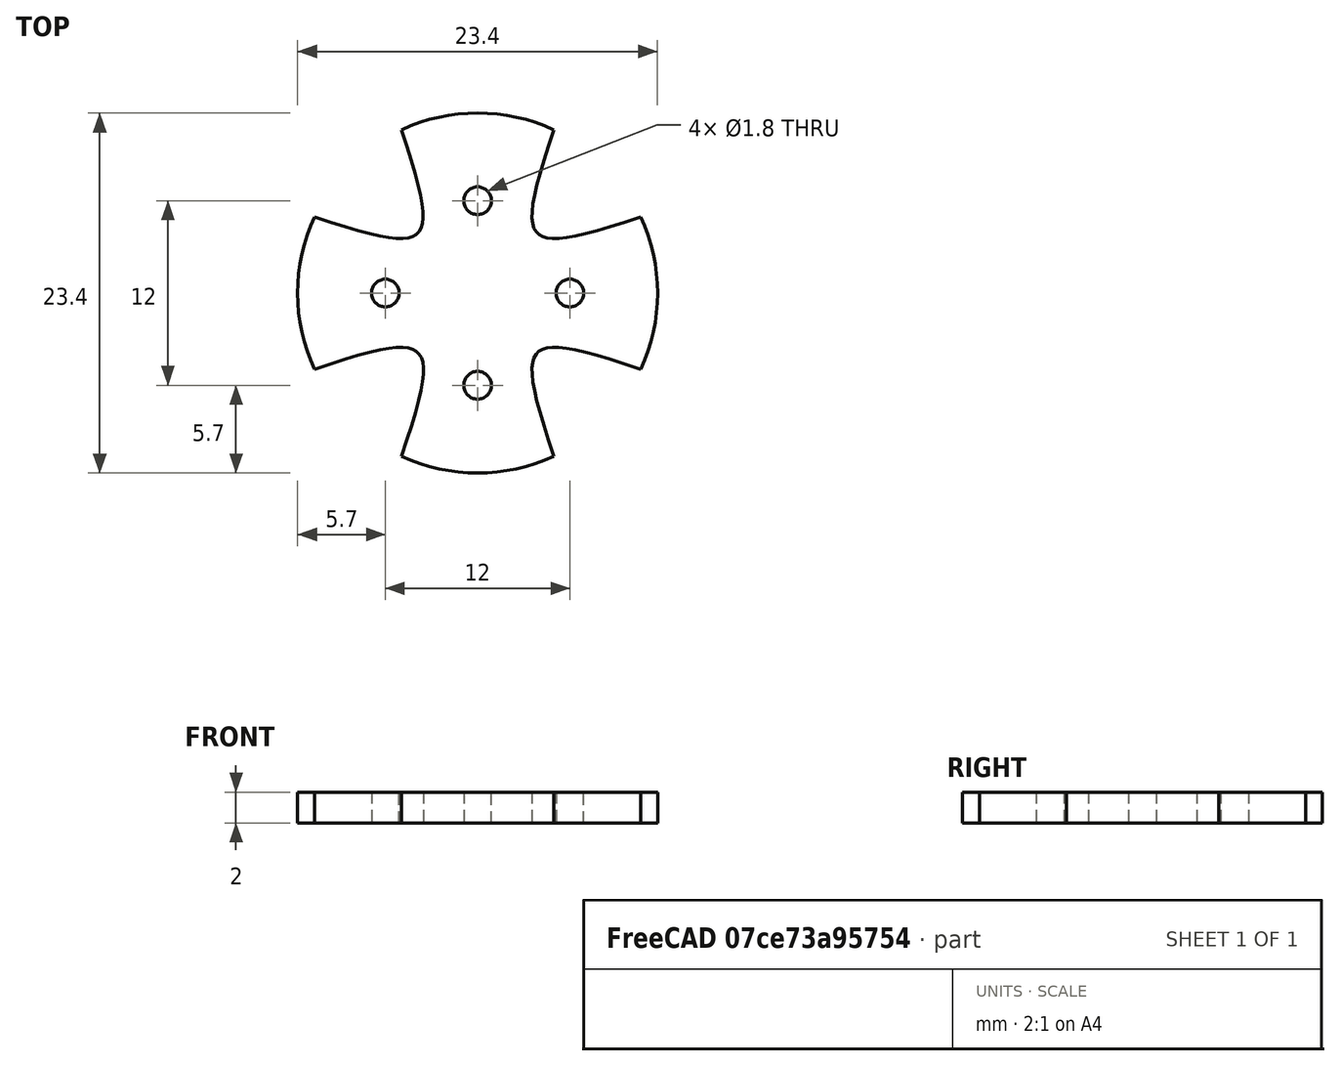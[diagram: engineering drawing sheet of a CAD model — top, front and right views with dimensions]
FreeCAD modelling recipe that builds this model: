
FCSTD DOCUMENT  (FreeCAD 0.19R0.19.2)
Label: boatMoterHolder010
License: All rights reserved
LicenseURL: http://en.wikipedia.org/wiki/All_rights_reserved
objects: Sketcher::SketchObject×2, Part::Extrusion×1
note: 3 computed .brp shape members not serialized (recipe doc carries the construction recipe); baked Part::Feature solids carry a one-line shape summary decoded from their .brp

FEATURE [Sketcher::SketchObject] Sketch
  FullyConstrained = true
  sketch-geometry (44):
    g0: Circle CenterX=-6 CenterY=0 CenterZ=0 NormalX=0 NormalY=0 NormalZ=1 AngleXU=0 Radius=0.9
    g1: Circle CenterX=0 CenterY=6 CenterZ=0 NormalX=0 NormalY=0 NormalZ=1 AngleXU=0 Radius=0.9
    g2: Circle CenterX=6 CenterY=0 CenterZ=0 NormalX=0 NormalY=0 NormalZ=1 AngleXU=0 Radius=0.9
    g3: Circle CenterX=0 CenterY=-6 CenterZ=0 NormalX=0 NormalY=0 NormalZ=1 AngleXU=0 Radius=0.9
    g4-g8: Circle x5 (B-spline internal-alignment scaffolding for g9; pole/knot coordinates omitted)
    g9: BSplineCurve PolesCount=5 KnotsCount=3 Degree=3 IsPeriodic=0
    g10: GeomPoint X=-4.94974 Y=10.6066 Z=0
    g11: GeomPoint X=-3.88908 Y=3.88909 Z=0
    g12: GeomPoint X=-10.6066 Y=4.94975 Z=0
    g13-g17: Circle x5 (B-spline internal-alignment scaffolding for g18; pole/knot coordinates omitted)
    g18: BSplineCurve PolesCount=5 KnotsCount=3 Degree=3 IsPeriodic=0
    g19: GeomPoint X=-10.6066 Y=-4.94974 Z=0
    g20: GeomPoint X=-3.88212 Y=-3.88197 Z=0
    g21: GeomPoint X=-4.94053 Y=-10.6109 Z=0
    g22-g26: Circle x5 (B-spline internal-alignment scaffolding for g27; pole/knot coordinates omitted)
    g27: BSplineCurve PolesCount=5 KnotsCount=3 Degree=3 IsPeriodic=0
    g28: GeomPoint X=4.94975 Y=-10.6066 Z=0
    g29: GeomPoint X=3.8852 Y=-3.88525 Z=0
    g30: GeomPoint X=10.603 Y=-4.95737 Z=0
    g31-g35: Circle x5 (B-spline internal-alignment scaffolding for g36; pole/knot coordinates omitted)
    g36: BSplineCurve PolesCount=5 KnotsCount=3 Degree=3 IsPeriodic=0
    g37: GeomPoint X=10.6066 Y=4.94975 Z=0
    g38: GeomPoint X=3.8891 Y=3.88908 Z=0
    g39: GeomPoint X=4.94975 Y=10.6066 Z=0
    g40: ArcOfCircle CenterX=0 CenterY=0 CenterZ=0 NormalX=0 NormalY=0 NormalZ=1 AngleXU=0 Radius=11.7047 StartAngle=1.13417 EndAngle=2.00742
    g41: ArcOfCircle CenterX=0 CenterY=0 CenterZ=0 NormalX=0 NormalY=0 NormalZ=1 AngleXU=0 Radius=11.7047 StartAngle=5.84584 EndAngle=6.71981
    g42: ArcOfCircle CenterX=0 CenterY=0 CenterZ=0 NormalX=0 NormalY=0 NormalZ=1 AngleXU=0 Radius=11.7047 StartAngle=4.27663 EndAngle=5.14902
    g43: ArcOfCircle CenterX=0 CenterY=0 CenterZ=0 NormalX=0 NormalY=0 NormalZ=1 AngleXU=0 Radius=11.7047 StartAngle=2.70497 EndAngle=3.57822
  constraints (50):
    c: Block(g1)
    c: Block(g2)
    c: Block(g3)
    c: Block(g0)
    c: Weight(g4) = 1
    c: Equal(g4, g5-g8) x4
    c: InternalAlignment(g4-g8 -> g9) x5
    c: InternalAlignment(g10,g9)
    c: InternalAlignment(g11,g9)
    c: InternalAlignment(g12,g9)
    c: Weight(g13) = 1
    c: Equal(g13, g14-g17) x4
    c: InternalAlignment(g13-g17 -> g18) x5
    c: InternalAlignment(g19,g18)
    c: InternalAlignment(g20,g18)
    c: InternalAlignment(g21,g18)
    c: Weight(g22) = 1
    c: Equal(g22,g24)
    c: Equal(g22,g25)
    c: Equal(g22,g26)
    c: InternalAlignment(g22-g26 -> g27) x5
    c: InternalAlignment(g28,g27)
    c: InternalAlignment(g29,g27)
    c: InternalAlignment(g30,g27)
    c: Weight(g31) = 1
    c: Equal(g31, g32-g35) x4
    c: InternalAlignment(g31-g35 -> g36) x5
    c: InternalAlignment(g37,g36)
    c: InternalAlignment(g38,g36)
    c: InternalAlignment(g39,g36)
    c: Coincident(g40,g-1)
    c: Coincident(g40,g9)
    c: Coincident(g40,g36)
    c: Coincident(g41,g40)
    c: Coincident(g41,g36)
    c: Coincident(g41,g27)
    c: Coincident(g42,g40)
    c: Coincident(g42,g27)
    c: Coincident(g42,g18)
    c: Coincident(g43,g40)
    c: Coincident(g43,g18)
    c: Coincident(g43,g9)
    c: Block(g41)
    c: Block(g40)
    c: Block(g43)
    c: Block(g42)
    c: Block(g36)
    c: Block(g9)
    c: Block(g27)
    c: Block(g18)
FEATURE [Part::Extrusion] Extrude
  Base = -> Sketch
  Dir = (0,0,1)
  DirMode = 2
  FaceMakerClass = Part::FaceMakerBullseye
  LengthFwd = 2
  LengthRev = 0
  Solid = true
  Symmetric = false
FEATURE [Sketcher::SketchObject] Sketch001
  FullyConstrained = false
  sketch-geometry (24):
    g0: Circle CenterX=-6 CenterY=0 CenterZ=0 NormalX=0 NormalY=0 NormalZ=1 AngleXU=0 Radius=0.9
    g1: Circle CenterX=6 CenterY=0 CenterZ=0 NormalX=0 NormalY=0 NormalZ=1 AngleXU=0 Radius=0.9
    g2: Circle CenterX=0 CenterY=-6 CenterZ=0 NormalX=0 NormalY=0 NormalZ=1 AngleXU=0 Radius=0.9
    g3: ArcOfCircle CenterX=0 CenterY=0 CenterZ=0 NormalX=0 NormalY=0 NormalZ=1 AngleXU=0 Radius=11.7047 StartAngle=1.13417 EndAngle=1.50239
    g4: ArcOfCircle CenterX=0 CenterY=0 CenterZ=0 NormalX=0 NormalY=0 NormalZ=1 AngleXU=0 Radius=11.7047 StartAngle=5.84584 EndAngle=6.21478
    g5: ArcOfCircle CenterX=0 CenterY=0 CenterZ=0 NormalX=0 NormalY=0 NormalZ=1 AngleXU=0 Radius=11.7047 StartAngle=4.27663 EndAngle=4.64399
    g6: ArcOfCircle CenterX=0 CenterY=0 CenterZ=0 NormalX=0 NormalY=0 NormalZ=1 AngleXU=0 Radius=11.7047 StartAngle=2.70497 EndAngle=3.07319
    g7: LineSegment StartX=22.4 StartY=-0.8 StartZ=0 EndX=11.6773 EndY=-0.8 EndZ=0
    g8: LineSegment StartX=22.4 StartY=0.8 StartZ=0 EndX=11.6773 EndY=0.8 EndZ=0
    g9: LineSegment StartX=0.8 StartY=22.4 StartZ=0 EndX=0.8 EndY=11.6773 EndZ=0
    g10: LineSegment StartX=-0.8 StartY=22.4 StartZ=0 EndX=-0.8 EndY=11.6773 EndZ=0
    g11: LineSegment StartX=-22.4 StartY=0.8 StartZ=0 EndX=-11.6773 EndY=0.8 EndZ=0
    g12: LineSegment StartX=-22.4 StartY=-0.8 StartZ=0 EndX=-11.6773 EndY=-0.8 EndZ=0
    g13: LineSegment StartX=-22.4 StartY=0.8 StartZ=0 EndX=-22.4 EndY=-0.8 EndZ=0
    g14: ArcOfCircle CenterX=0 CenterY=0 CenterZ=0 NormalX=0 NormalY=0 NormalZ=1 AngleXU=0 Radius=11.7047 StartAngle=3.20999 EndAngle=3.57822
    g15: ArcOfCircle CenterX=0 CenterY=0 CenterZ=0 NormalX=0 NormalY=0 NormalZ=1 AngleXU=0 Radius=11.7047 StartAngle=1.6392 EndAngle=2.00742
    g16: ArcOfCircle CenterX=0 CenterY=0 CenterZ=0 NormalX=0 NormalY=0 NormalZ=1 AngleXU=0 Radius=11.7047 StartAngle=0.0684019 EndAngle=0.436627
    g17: LineSegment StartX=-0.8 StartY=22.4 StartZ=0 EndX=0.8 EndY=22.4 EndZ=0
    g18: LineSegment StartX=22.4 StartY=-0.8 StartZ=0 EndX=22.4 EndY=0.8 EndZ=0
    g19: LineSegment StartX=0.8 StartY=-22.4 StartZ=0 EndX=0.8 EndY=-11.6773 EndZ=0
    g20: LineSegment StartX=-0.8 StartY=-22.4 StartZ=0 EndX=-0.8 EndY=-11.6773 EndZ=0
    g21: LineSegment StartX=-0.8 StartY=-22.4 StartZ=0 EndX=0.8 EndY=-22.4 EndZ=0
    g22: ArcOfCircle CenterX=0 CenterY=0 CenterZ=0 NormalX=0 NormalY=0 NormalZ=1 AngleXU=0 Radius=11.7047 StartAngle=4.78079 EndAngle=5.14902
    g23: LineSegment StartX=0 StartY=6 StartZ=0 EndX=0 EndY=8.9 EndZ=0
  constraints (65):
    c: Block(g1)
    c: Block(g2)
    c: Block(g0)
    c: Coincident(g3,g-1)
    c: Coincident(g4,g3)
    c: Coincident(g5,g3)
    c: Coincident(g6,g3)
    c: Block(g4)
    c: Block(g3)
    c: Block(g6)
    c: Block(g5)
    c: Horizontal(g7)
    c: Horizontal(g8)
    c: Vertical(g9)
    c: Vertical(g10)
    c: Horizontal(g11)
    c: Horizontal(g12)
    c: Block(g12)
    c: Block(g11)
    c: Block(g10)
    c: Block(g9)
    c: Block(g8)
    c: Block(g7)
    c: Coincident(g13,g11)
    c: Coincident(g13,g12)
    c: Vertical(g13)
    c: Distance(g13) = 1.6
    c: Equal(g6,g14)
    c: Coincident(g6,g11)
    c: Coincident(g14,g12)
    c: Coincident(g6,g14)
    c: Equal(g3,g15)
    c: Coincident(g3,g9)
    c: Coincident(g15,g10)
    c: Coincident(g3,g15)
    c: Equal(g4,g16)
    c: Coincident(g4,g7)
    c: PointOnObject(g16,g8)
    c: Coincident(g4,g16)
    c: Coincident(g17,g10)
    c: Coincident(g17,g9)
    c: Horizontal(g17)
    c: Distance(g17) = 1.6
    c: Coincident(g18,g7)
    c: Coincident(g18,g8)
    c: Vertical(g18)
    c: Distance(g18) = 1.6
    c: Vertical(g19)
    c: Vertical(g20)
    c: Block(g19)
    c: Block(g20)
    c: Coincident(g21,g20)
    c: Coincident(g21,g19)
    c: Horizontal(g21)
    c: Equal(g5,g22)
    c: Coincident(g5,g20)
    c: Coincident(g22,g19)
    c: Coincident(g5,g22)
    c: PointOnObject(g23,g-2)
    c: Vertical(g23)
    c: Distance(g23) = 2.9
    c: Block(g14)
    c: Block(g15)
    c: Block(g16)
    c: Block(g22)
